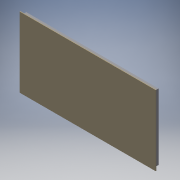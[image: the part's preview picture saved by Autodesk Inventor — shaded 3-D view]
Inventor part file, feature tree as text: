
AUTODESK INVENTOR PART (.ipt)
format: ipt  version: 2019 (Build 230136000, 136)  size: 99,840 bytes
history: native  units: mm
features: other x6, reference x4, extrude x2, sketch x2
ambient origin geometry x8: Origin, YZ Plane, XZ Plane, XY Plane, X Axis, Y Axis, Z Axis, Center Point
bodies: Solid1 (feature_tree)
feature tree (14):
  extrude  "Extrusion1"  Depth=861.06mm
  extrude  "Extrusion2"  Depth=25.4mm TaperAngle=0.0deg
  sketch  "Sketch1"  dims[d0=4.7625mm d1=0.0mm d2=861.06mm]
  sketch  "Sketch2"  dims[d3=444.5mm d4=25.4mm d5=0.0mm]
  reference  "Reference1"
  reference  "Reference2"
  reference  "Reference3"
  reference  "Reference4"
  parser-record x1  (decoder bookkeeping rows leaked as tree rows — omitted from the tree; the rows remain in map.json)
  other  "enclosure.iam"
  other  "1515-S-BLACK_rear_vert_post:1"
  other  "1515-S-BLACK_side_long_top:1"
  other  "1530-S-BLACK_base_side:2"
  other  "1515-S-BLACK_front_vert_post:1"
note: 1 file-system path scrubbed to <path> (originals preserved in map.json)
